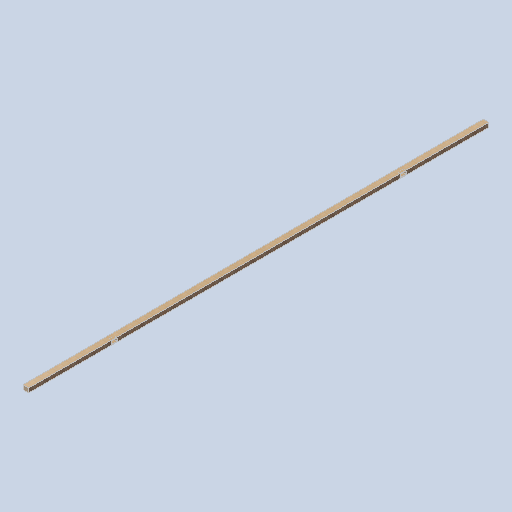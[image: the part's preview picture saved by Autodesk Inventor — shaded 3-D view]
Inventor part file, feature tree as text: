
AUTODESK INVENTOR PART (.ipt)
format: ipt  version: 2024.2 (Build 282272000, 272)  size: 280,064 bytes
history: native  units: mm
features: extrude x2, sketch x2
ambient origin geometry x8: Origin, YZ Plane, XZ Plane, XY Plane, X Axis, Y Axis, Z Axis, Center Point
bodies: Solid1 (feature_tree)
feature tree (4):
  extrude  "Extrusion1"  Depth=400.0mm
  extrude  "Extrusion2"  Depth=200.0mm TaperAngle=0.0deg
  sketch  "Sketch1"  dims[d0=32302.0mm d1=0.0mm d3=400.0mm]
  sketch  "Sketch2"  dims[d4=200.0mm d5=200.0mm d6=0.0mm]
